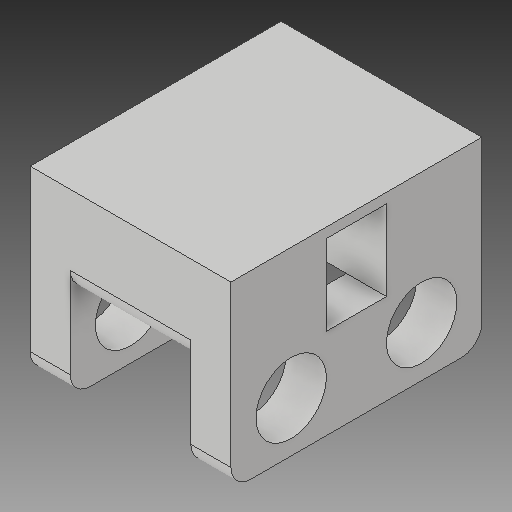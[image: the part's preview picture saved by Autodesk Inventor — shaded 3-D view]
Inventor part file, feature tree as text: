
AUTODESK INVENTOR PART (.ipt)
format: ipt  version: 2019 (Build 230136000, 136)  size: 160,768 bytes
history: native  units: mm
features: sketch x3, extrude x2, hole x1, plane x1, mirror x1, fillet x1
ambient origin geometry x8: Origin, YZ Plane, XZ Plane, XY Plane, X Axis, Y Axis, Z Axis, Center Point
bodies: Solid1 (feature_tree)
feature tree (9):
  extrude  "Extrusion1"  Depth=20.0mm
  hole  "Hole1"  [1 undecoded]
  plane  "Work Plane1"
  mirror  "Mirror1"
  fillet  "Fillet1"  Radius=5.0mm
  extrude  "Extrusion2"  Depth=4.0mm
  sketch  "Sketch1"  dims[d0=18.0mm d1=20.0mm]
  sketch  "Sketch2"  dims[d2=9.0mm d6=25.0mm d7=0.0mm d10=5.0mm]
  sketch  "Sketch3"  dims[d11=6.0mm d12=7.0mm d13=6.0mm d14=4.0mm d15=2.0mm d16=90.0deg d17=8.0mm d18=20.594885mm d19=12.5mm d20=2.0mm d21=6.0mm d22=8.0mm d24=9.0mm d25=9.5mm d26=20.0mm d27=0.0mm d28=12.0mm d29=4.0mm d30=4.0mm]
note: 1 required parameter value undecoded (feature->parameter linkage not recoverable at this tier; creation-order binding heuristic only, values carry confidence <= 0.55)
